# Revit family: QF_BOURGEAT_Rayonnage_modulaire_étagère_de_base
name_source: partatom
category: Equipement spécialisé
revit_build: Autodesk Revit 2015 (Build: 20140606_1530(x64)
units: mm (PartAtom-declared; Revit-internal decimal feet)

## types (38) — shared parameters
4 niveaux Plateau 2 = Non
4 niveaux plateau 3 = Non

## per-type parameters (varying)
| type | 4 niveaux | Calagepl2 | Calagepl3 | LP1 | LP2 | LP3 | Longueur | Longueur Plateau 1 | Longueur Plateau 2 | Longueur Plateau 3 | Modèle | Plateau 2 | Plateau 3 | Profondeur |
| 805x425 3N | Non | 0 mm  [stored 0 ft] | 0 mm  [stored 0 ft] | 1 | 0 | 0 | 805 mm  [stored 2.64108 ft] | 805 mm  [stored 2.64108 ft] | 805 mm  [stored 2.64108 ft] | 805 mm  [stored 2.64108 ft] | 801308 | Non | Non | 425 mm |
| 805x425 4N | Oui | 0 mm  [stored 0 ft] | 0 mm  [stored 0 ft] | 1 | 0 | 0 | 805 mm  [stored 2.64108 ft] | 805 mm  [stored 2.64108 ft] | 805 mm  [stored 2.64108 ft] | 805 mm  [stored 2.64108 ft] | 801408 | Non | Non | 425 mm |
| 805x600 3N | Non | 0 mm  [stored 0 ft] | 0 mm  [stored 0 ft] | 1 | 0 | 0 | 805 mm  [stored 2.64108 ft] | 805 mm  [stored 2.64108 ft] | 805 mm  [stored 2.64108 ft] | 805 mm  [stored 2.64108 ft] | 802308 | Non | Non | 600 mm  [stored 1.9685 ft] |
| 805x600 4N | Oui | 0 mm  [stored 0 ft] | 0 mm  [stored 0 ft] | 1 | 0 | 0 | 805 mm  [stored 2.64108 ft] | 805 mm  [stored 2.64108 ft] | 805 mm  [stored 2.64108 ft] | 805 mm  [stored 2.64108 ft] | 802408 | Non | Non | 600 mm  [stored 1.9685 ft] |
| 910x425 3N | Non | 0 mm  [stored 0 ft] | 0 mm  [stored 0 ft] | 2 | 0 | 0 | 910 mm | 910 mm | 805 mm  [stored 2.64108 ft] | 805 mm  [stored 2.64108 ft] | 801309 | Non | Non | 425 mm |
| 910x425 4N | Oui | 0 mm  [stored 0 ft] | 0 mm  [stored 0 ft] | 2 | 0 | 0 | 910 mm | 910 mm | 805 mm  [stored 2.64108 ft] | 805 mm  [stored 2.64108 ft] | 801409 | Non | Non | 425 mm |
| 910x600 3N | Non | 0 mm  [stored 0 ft] | 0 mm  [stored 0 ft] | 2 | 0 | 0 | 910 mm | 910 mm | 805 mm  [stored 2.64108 ft] | 805 mm  [stored 2.64108 ft] | 802309 | Non | Non | 600 mm  [stored 1.9685 ft] |
| 910x600 4N | Oui | 0 mm  [stored 0 ft] | 0 mm  [stored 0 ft] | 2 | 0 | 0 | 910 mm | 910 mm | 805 mm  [stored 2.64108 ft] | 805 mm  [stored 2.64108 ft] | 802409 | Non | Non | 600 mm  [stored 1.9685 ft] |
| 1020x425 3N | Non | 0 mm  [stored 0 ft] | 0 mm  [stored 0 ft] | 3 | 0 | 0 | 1020 mm  [stored 3.34646 ft] | 1020 mm  [stored 3.34646 ft] | 805 mm  [stored 2.64108 ft] | 805 mm  [stored 2.64108 ft] | 801310 | Non | Non | 425 mm |
| 1020x425 4N | Oui | 0 mm  [stored 0 ft] | 0 mm  [stored 0 ft] | 3 | 0 | 0 | 1020 mm  [stored 3.34646 ft] | 1020 mm  [stored 3.34646 ft] | 805 mm  [stored 2.64108 ft] | 805 mm  [stored 2.64108 ft] | 801410 | Non | Non | 425 mm |
| 1020x600 3N | Non | 0 mm  [stored 0 ft] | 0 mm  [stored 0 ft] | 3 | 0 | 0 | 1020 mm  [stored 3.34646 ft] | 1020 mm  [stored 3.34646 ft] | 805 mm  [stored 2.64108 ft] | 805 mm  [stored 2.64108 ft] | 802310 | Non | Non | 600 mm  [stored 1.9685 ft] |
| 1020x600 4N | Oui | 0 mm  [stored 0 ft] | 0 mm  [stored 0 ft] | 3 | 0 | 0 | 1020 mm  [stored 3.34646 ft] | 1020 mm  [stored 3.34646 ft] | 805 mm  [stored 2.64108 ft] | 805 mm  [stored 2.64108 ft] | 802410 | Non | Non | 600 mm  [stored 1.9685 ft] |
| 1125x425 3N | Non | 0 mm  [stored 0 ft] | 0 mm  [stored 0 ft] | 4 | 0 | 0 | 1125 mm | 1125 mm | 805 mm  [stored 2.64108 ft] | 805 mm  [stored 2.64108 ft] | 801311 | Non | Non | 425 mm |
| 1125x425 4N | Oui | 0 mm  [stored 0 ft] | 0 mm  [stored 0 ft] | 4 | 0 | 0 | 1125 mm | 1125 mm | 805 mm  [stored 2.64108 ft] | 805 mm  [stored 2.64108 ft] | 801411 | Non | Non | 425 mm |
| 1125x600 3N | Non | 0 mm  [stored 0 ft] | 0 mm  [stored 0 ft] | 4 | 0 | 0 | 1125 mm | 1125 mm | 805 mm  [stored 2.64108 ft] | 805 mm  [stored 2.64108 ft] | 802311 | Non | Non | 600 mm  [stored 1.9685 ft] |
| 1125x600 4N | Oui | 0 mm  [stored 0 ft] | 0 mm  [stored 0 ft] | 4 | 0 | 0 | 1125 mm | 1125 mm | 805 mm  [stored 2.64108 ft] | 805 mm  [stored 2.64108 ft] | 802411 | Non | Non | 600 mm  [stored 1.9685 ft] |
| 1235x425 3N | Non | 0 mm  [stored 0 ft] | 0 mm  [stored 0 ft] | 5 | 0 | 0 | 1235 mm  [stored 4.05184 ft] | 1235 mm  [stored 4.05184 ft] | 805 mm  [stored 2.64108 ft] | 805 mm  [stored 2.64108 ft] | 801312 | Non | Non | 425 mm |
| 1235x425 4N | Oui | 0 mm  [stored 0 ft] | 0 mm  [stored 0 ft] | 5 | 0 | 0 | 1235 mm  [stored 4.05184 ft] | 1235 mm  [stored 4.05184 ft] | 805 mm  [stored 2.64108 ft] | 805 mm  [stored 2.64108 ft] | 801412 | Non | Non | 425 mm |
| 1235x600 3N | Non | 0 mm  [stored 0 ft] | 0 mm  [stored 0 ft] | 5 | 0 | 0 | 1235 mm  [stored 4.05184 ft] | 1235 mm  [stored 4.05184 ft] | 805 mm  [stored 2.64108 ft] | 805 mm  [stored 2.64108 ft] | 802312 | Non | Non | 600 mm  [stored 1.9685 ft] |
| 1235x600 4N | Oui | 0 mm  [stored 0 ft] | 0 mm  [stored 0 ft] | 5 | 0 | 0 | 1235 mm  [stored 4.05184 ft] | 1235 mm  [stored 4.05184 ft] | 805 mm  [stored 2.64108 ft] | 805 mm  [stored 2.64108 ft] | 802412 | Non | Non | 600 mm  [stored 1.9685 ft] |
| 1345x425 3N | Non | 0 mm  [stored 0 ft] | 0 mm  [stored 0 ft] | 6 | 0 | 0 | 1345 mm | 1345 mm | 805 mm  [stored 2.64108 ft] | 805 mm  [stored 2.64108 ft] | 801313 | Non | Non | 425 mm |
| 1345x425 4N | Oui | 0 mm  [stored 0 ft] | 0 mm  [stored 0 ft] | 6 | 0 | 0 | 1345 mm | 1345 mm | 805 mm  [stored 2.64108 ft] | 805 mm  [stored 2.64108 ft] | 801413 | Non | Non | 425 mm |
| 1345x600 3N | Non | 0 mm  [stored 0 ft] | 0 mm  [stored 0 ft] | 6 | 0 | 0 | 1345 mm | 1345 mm | 805 mm  [stored 2.64108 ft] | 805 mm  [stored 2.64108 ft] | 802313 | Non | Non | 600 mm  [stored 1.9685 ft] |
| 1345x600 4N | Oui | 0 mm  [stored 0 ft] | 0 mm  [stored 0 ft] | 6 | 0 | 0 | 1345 mm | 1345 mm | 805 mm  [stored 2.64108 ft] | 805 mm  [stored 2.64108 ft] | 802413 | Non | Non | 600 mm  [stored 1.9685 ft] |
| 1450x425 3N | Non | 0 mm  [stored 0 ft] | 0 mm  [stored 0 ft] | 7 | 0 | 0 | 1450 mm  [stored 4.75722 ft] | 1450 mm  [stored 4.75722 ft] | 805 mm  [stored 2.64108 ft] | 805 mm  [stored 2.64108 ft] | 801314 | Non | Non | 425 mm |
| 1450x425 4N | Oui | 0 mm  [stored 0 ft] | 0 mm  [stored 0 ft] | 7 | 0 | 0 | 1450 mm  [stored 4.75722 ft] | 1450 mm  [stored 4.75722 ft] | 805 mm  [stored 2.64108 ft] | 805 mm  [stored 2.64108 ft] | 801414 | Non | Non | 425 mm |
| 1450x600 3N | Non | 0 mm  [stored 0 ft] | 0 mm  [stored 0 ft] | 7 | 0 | 0 | 1450 mm  [stored 4.75722 ft] | 1450 mm  [stored 4.75722 ft] | 805 mm  [stored 2.64108 ft] | 805 mm  [stored 2.64108 ft] | 802314 | Non | Non | 600 mm  [stored 1.9685 ft] |
| 1450x600 4N | Oui | 0 mm  [stored 0 ft] | 0 mm  [stored 0 ft] | 7 | 0 | 0 | 1450 mm  [stored 4.75722 ft] | 1450 mm  [stored 4.75722 ft] | 805 mm  [stored 2.64108 ft] | 805 mm  [stored 2.64108 ft] | 802414 | Non | Non | 600 mm  [stored 1.9685 ft] |
| 1560x425 3N | Non | 0 mm  [stored 0 ft] | 0 mm  [stored 0 ft] | 8 | 0 | 0 | 1560 mm  [stored 5.11811 ft] | 1560 mm  [stored 5.11811 ft] | 805 mm  [stored 2.64108 ft] | 805 mm  [stored 2.64108 ft] | 801315 | Non | Non | 425 mm |
| 1560x425 4N | Oui | 0 mm  [stored 0 ft] | 0 mm  [stored 0 ft] | 8 | 0 | 0 | 1560 mm  [stored 5.11811 ft] | 1560 mm  [stored 5.11811 ft] | 805 mm  [stored 2.64108 ft] | 805 mm  [stored 2.64108 ft] | 801415 | Non | Non | 425 mm |
| 1560x600 3N | Non | 0 mm  [stored 0 ft] | 0 mm  [stored 0 ft] | 8 | 0 | 0 | 1560 mm  [stored 5.11811 ft] | 1560 mm  [stored 5.11811 ft] | 805 mm  [stored 2.64108 ft] | 805 mm  [stored 2.64108 ft] | 802315 | Non | Non | 600 mm  [stored 1.9685 ft] |
| 1560x600 4N | Oui | 0 mm  [stored 0 ft] | 0 mm  [stored 0 ft] | 8 | 0 | 0 | 1560 mm  [stored 5.11811 ft] | 1560 mm  [stored 5.11811 ft] | 805 mm  [stored 2.64108 ft] | 805 mm  [stored 2.64108 ft] | 802415 | Non | Non | 600 mm  [stored 1.9685 ft] |
| 1670x425 3N | Non | 0 mm  [stored 0 ft] | 0 mm  [stored 0 ft] | 9 | 0 | 0 | 1670 mm | 1670 mm | 805 mm  [stored 2.64108 ft] | 805 mm  [stored 2.64108 ft] | 801316 | Non | Non | 425 mm |
| 1670x425 4N | Oui | 0 mm  [stored 0 ft] | 0 mm  [stored 0 ft] | 9 | 0 | 0 | 1670 mm | 1670 mm | 805 mm  [stored 2.64108 ft] | 805 mm  [stored 2.64108 ft] | 801416 | Non | Non | 425 mm |
| 1670x600 3N | Non | 0 mm  [stored 0 ft] | 0 mm  [stored 0 ft] | 9 | 0 | 0 | 1670 mm | 1670 mm | 805 mm  [stored 2.64108 ft] | 805 mm  [stored 2.64108 ft] | 802316 | Non | Non | 600 mm  [stored 1.9685 ft] |
| 1670x600 4N | Oui | 0 mm  [stored 0 ft] | 0 mm  [stored 0 ft] | 9 | 0 | 0 | 1670 mm | 1670 mm | 805 mm  [stored 2.64108 ft] | 805 mm  [stored 2.64108 ft] | 802416 | Non | Non | 600 mm  [stored 1.9685 ft] |
| 2325x425 3N | Non | 1104 mm | 0 mm  [stored 0 ft] | 4 | 5 | 0 | 2325 mm | 1125 mm | 1235 mm  [stored 4.05184 ft] | 805 mm  [stored 2.64108 ft] | 801323 | Oui | Non | 425 mm |
| 3530x425 3N | Non | 1104 mm | 2187 mm | 4 | 4 | 6 | 3530 mm | 1125 mm | 1125 mm | 1345 mm | 801335 | Oui | Oui | 425 mm |

note: [stored X ft] marks values corroborated as IEEE doubles in the binary element streams (Revit-internal decimal feet)
